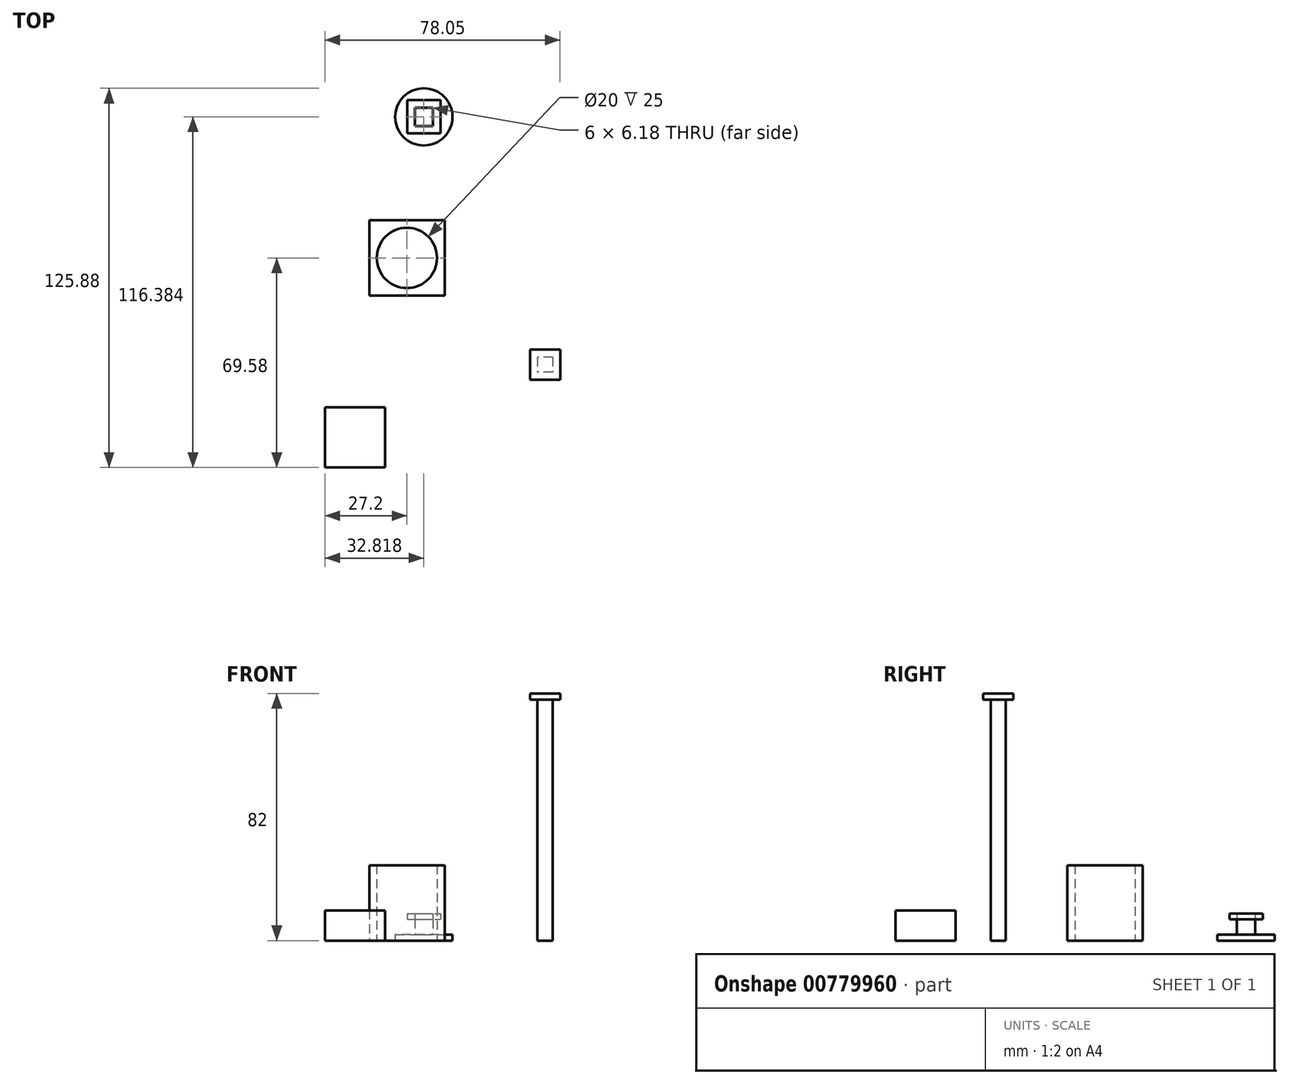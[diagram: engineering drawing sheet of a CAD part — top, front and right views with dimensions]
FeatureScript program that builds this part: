
annotation { "Feature Type Name" : "Feature", "Feature Type Description" : "" }
export const myFeature = defineFeature(function(context is Context, id is Id, definition is map)
    precondition{}
    {
        {
            var Q0;
            Q0=qCreatedBy(makeId("Top.planeOp"),FACE);
            var sketch = newSketch(context, id + "F0", { "sketchPlane" : qUnion([Q0])});
            skLineSegment(sketch, "E0.bottom", {"start": v(12.5, -12.5) * mm, "end": v(-12.5, -12.5) * mm});
            skLineSegment(sketch, "E0.top", {"start": v(12.5, 12.5) * mm, "end": v(-12.5, 12.5) * mm});
            skLineSegment(sketch, "E0.left", {"start": v(12.5, -12.5) * mm, "end": v(12.5, 12.5) * mm});
            skLineSegment(sketch, "E0.right", {"start": v(-12.5, -12.5) * mm, "end": v(-12.5, 12.5) * mm});
            skPoint(sketch, "E0.middle", {"position": v(0, 0) * mm});
            skSolve(sketch);
        }
        {
            var Q0;
            Q0=makeQuery(id+"F0.imprint","IMPRINT",FACE,{"disambiguationData":[TD([[makeQuery(id+"F0.imprint","IMPRINT",EDGE,{"derivedFrom":sQuery(id+"F0.wireOp",EDGE,"E0.bottom")}),-1.0]])]});
            extrude(context, id + "F1", {"entities" : qUnion([Q0]), "depth" : 25 * mm, "offsetDistance" : 25 * mm});
        }
        {
            var Q0;
            Q0=sQuery(id+"F0.wireOp",VERTEX,"E0.middle");
            var Q1;
            Q1=makeQuery(id+"F1.opExtrude","SWEPT_BODY",BODY,{"disambiguationData":[OSD([sQuery(id+"F0.wireOp",EDGE,"E0.bottom"),sQuery(id+"F0.wireOp",EDGE,"E0.top"),sQuery(id+"F0.wireOp",EDGE,"E0.left"),sQuery(id+"F0.wireOp",EDGE,"E0.right")])]});
            hole(context, id + "F2", {"style" : HoleStyle.SIMPLE, "endStyle" : HoleEndStyle.THROUGH, "oppositeDirection" : true, "holeDiameter" : 20 * mm, "majorDiameter" : 5 * mm, "isTappedThrough" : true, "tappedDepth" : 12 * mm, "tapClearance" : 3, "locations" : qUnion([Q0]), "scope" : qUnion([Q1])});
        }
        {
            var Q0;
            Q0=qCreatedBy(makeId("Top.planeOp"),FACE);
            var sketch = newSketch(context, id + "F3", { "sketchPlane" : qUnion([Q0])});
            skCircle(sketch, "E1", {"center": v(5.62, 46.8) * mm, "radius": 9.5 * mm});
            skSolve(sketch);
        }
        {
            var Q0;
            Q0 = qSketchRegion(id + "F3", true);
            extrude(context, id + "F4", {"entities" : qUnion([Q0]), "depth" : 2 * mm, "offsetDistance" : 25 * mm});
        }
        {
            var Q0;
            Q0=makeQuery(id+"F4.opExtrude","CAP_FACE",FACE,{"disambiguationData":[OSD([sQuery(id+"F3.wireOp",EDGE,"E1")])],"isStart":false});
            var sketch = newSketch(context, id + "F5", { "sketchPlane" : qUnion([Q0])});
            skLineSegment(sketch, "E2.bottom", {"start": v(2.62, 49.9) * mm, "end": v(8.62, 49.9) * mm});
            skLineSegment(sketch, "E2.top", {"start": v(2.62, 43.71) * mm, "end": v(8.62, 43.71) * mm});
            skLineSegment(sketch, "E2.left", {"start": v(2.62, 49.9) * mm, "end": v(2.62, 43.71) * mm});
            skLineSegment(sketch, "E2.right", {"start": v(8.62, 49.9) * mm, "end": v(8.62, 43.71) * mm});
            skPoint(sketch, "E2.middle", {"position": v(5.62, 46.8) * mm});
            skSolve(sketch);
        }
        {
            var Q0;
            Q0=makeQuery(id+"F5.imprint","IMPRINT",FACE,{"disambiguationData":[TD([[makeQuery(id+"F5.imprint","IMPRINT",EDGE,{"derivedFrom":sQuery(id+"F5.wireOp",EDGE,"E2.bottom")}),-1.0]])]});
            var Q1;
            Q1=sQuery(id+"F5.wireOp",EDGE,"E2.top");
            var Q2;
            Q2=sQuery(id+"F5.wireOp",EDGE,"E2.right");
            var Q3;
            Q3=sQuery(id+"F5.wireOp",EDGE,"E2.left");
            var Q4;
            Q4=sQuery(id+"F5.wireOp",EDGE,"E2.bottom");
            extrude(context, id + "F6", {"entities" : qUnion([Q0]), "operationType" : NewBodyOperationType.ADD, "surfaceOperationType" : NewSurfaceOperationType.ADD, "surfaceEntities" : qUnion([Q1, Q2, Q3, Q4]), "depth" : 5 * mm, "offsetDistance" : 25 * mm});
        }
        {
            var Q0;
            Q0=qCreatedBy(makeId("Top.planeOp"),FACE);
            var sketch = newSketch(context, id + "F7", { "sketchPlane" : qUnion([Q0])});
            skLineSegment(sketch, "E3.bottom", {"start": v(9.2, -50.91) * mm, "end": v(-5.8, -50.91) * mm});
            skLineSegment(sketch, "E3.top", {"start": v(9.2, -65.91) * mm, "end": v(-5.8, -65.91) * mm});
            skLineSegment(sketch, "E3.left", {"start": v(9.2, -50.91) * mm, "end": v(9.2, -65.91) * mm});
            skLineSegment(sketch, "E3.right", {"start": v(-5.8, -50.91) * mm, "end": v(-5.8, -65.91) * mm});
            skPoint(sketch, "E3.middle", {"position": v(1.7, -58.41) * mm});
            skSolve(sketch);
        }
        {
            var Q0;
            Q0 = qSketchRegion(id + "F7", true);
            extrude(context, id + "F8", {"entities" : qUnion([Q0]), "depth" : 80 * mm, "offsetDistance" : 25 * mm});
        }
        {
            var Q0;
            Q0=qCreatedBy(makeId("Top.planeOp"),FACE);
            var sketch = newSketch(context, id + "F9", { "sketchPlane" : qUnion([Q0])});
            skLineSegment(sketch, "E4.bottom", {"start": v(48.35, -32.97) * mm, "end": v(43.35, -32.97) * mm});
            skLineSegment(sketch, "E4.top", {"start": v(48.35, -37.97) * mm, "end": v(43.35, -37.97) * mm});
            skLineSegment(sketch, "E4.left", {"start": v(48.35, -32.97) * mm, "end": v(48.35, -37.97) * mm});
            skLineSegment(sketch, "E4.right", {"start": v(43.35, -32.97) * mm, "end": v(43.35, -37.97) * mm});
            skPoint(sketch, "E4.middle", {"position": v(45.85, -35.47) * mm});
            skSolve(sketch);
        }
        {
            var Q0;
            Q0 = qSketchRegion(id + "F9", true);
            extrude(context, id + "F10", {"entities" : qUnion([Q0]), "depth" : 80 * mm, "offsetDistance" : 25 * mm});
        }
        {
            var Q0;
            Q0=makeQuery(id+"F8.opExtrude","SWEPT_BODY",BODY,{"disambiguationData":[OSD([sQuery(id+"F7.wireOp",EDGE,"E3.bottom"),sQuery(id+"F7.wireOp",EDGE,"E3.top"),sQuery(id+"F7.wireOp",EDGE,"E3.left"),sQuery(id+"F7.wireOp",EDGE,"E3.right")])]});
            deleteBodies(context, id + "F11", {"entities" : qUnion([Q0])});
        }
        {
            var Q0;
            Q0=makeQuery(id+"F10.opExtrude","CAP_FACE",FACE,{"disambiguationData":[OSD([sQuery(id+"F9.wireOp",EDGE,"E4.bottom"),sQuery(id+"F9.wireOp",EDGE,"E4.top"),sQuery(id+"F9.wireOp",EDGE,"E4.left"),sQuery(id+"F9.wireOp",EDGE,"E4.right")])],"isStart":false});
            var sketch = newSketch(context, id + "F12", { "sketchPlane" : qUnion([Q0])});
            skLineSegment(sketch, "E5.bottom", {"start": v(50.85, -30.47) * mm, "end": v(40.85, -30.47) * mm});
            skLineSegment(sketch, "E5.top", {"start": v(50.85, -40.47) * mm, "end": v(40.85, -40.47) * mm});
            skLineSegment(sketch, "E5.left", {"start": v(50.85, -30.47) * mm, "end": v(50.85, -40.47) * mm});
            skLineSegment(sketch, "E5.right", {"start": v(40.85, -30.47) * mm, "end": v(40.85, -40.47) * mm});
            skPoint(sketch, "E5.middle", {"position": v(45.85, -35.47) * mm});
            skPoint(sketch, "E5.middle.positionSnap0", {"position": v(48.35, -35.47) * mm});
            skPoint(sketch, "E5.middle.positionSnap1", {"position": v(45.85, -32.97) * mm});
            skPoint(sketch, "E5.centerSnap0", {"position": v(48.35, -35.47) * mm});
            skPoint(sketch, "E5.centerSnap1", {"position": v(45.85, -32.97) * mm});
            skSolve(sketch);
        }
        {
            var Q0;
            Q0=makeQuery(id+"F12.imprint","IMPRINT",FACE,{"disambiguationData":[TD([[makeQuery(id+"F12.imprint","IMPRINT",EDGE,{"derivedFrom":makeQuery(id+"F10.opExtrude","CAP_EDGE",EDGE,{"disambiguationData":[OSD([sQuery(id+"F9.wireOp",EDGE,"E4.bottom")])],"isStart":false})}),1.0]])]});
            var Q1;
            Q1=makeQuery(id+"F12.imprint","IMPRINT",FACE,{"disambiguationData":[TD([[makeQuery(id+"F12.imprint","IMPRINT",EDGE,{"derivedFrom":sQuery(id+"F12.wireOp",EDGE,"E5.bottom")}),1.0]])]});
            extrude(context, id + "F13", {"entities" : qUnion([Q0, Q1]), "operationType" : NewBodyOperationType.ADD, "depth" : 2 * mm, "offsetDistance" : 25 * mm});
        }
        {
            var Q0;
            Q0=qCreatedBy(makeId("Top.planeOp"),FACE);
            var sketch = newSketch(context, id + "F14", { "sketchPlane" : qUnion([Q0])});
            skLineSegment(sketch, "E6.bottom", {"start": v(-7.2, -49.58) * mm, "end": v(-27.2, -49.58) * mm});
            skLineSegment(sketch, "E6.top", {"start": v(-7.2, -69.58) * mm, "end": v(-27.2, -69.58) * mm});
            skLineSegment(sketch, "E6.left", {"start": v(-7.2, -49.58) * mm, "end": v(-7.2, -69.58) * mm});
            skLineSegment(sketch, "E6.right", {"start": v(-27.2, -49.58) * mm, "end": v(-27.2, -69.58) * mm});
            skPoint(sketch, "E6.middle", {"position": v(-17.2, -59.58) * mm});
            skSolve(sketch);
        }
        {
            var Q0;
            Q0=makeQuery(id+"F14.imprint","IMPRINT",FACE,{"disambiguationData":[TD([[makeQuery(id+"F14.imprint","IMPRINT",EDGE,{"derivedFrom":sQuery(id+"F14.wireOp",EDGE,"E6.bottom")}),1.0]])]});
            extrude(context, id + "F15", {"entities" : qUnion([Q0]), "depth" : 10 * mm, "offsetDistance" : 25 * mm});
        }
        {
            var Q0;
            Q0=makeQuery(id+"F6.opExtrude","CAP_FACE",FACE,{"disambiguationData":[OSD([sQuery(id+"F5.wireOp",EDGE,"E2.bottom"),sQuery(id+"F5.wireOp",EDGE,"E2.top"),sQuery(id+"F5.wireOp",EDGE,"E2.left"),sQuery(id+"F5.wireOp",EDGE,"E2.right")])],"isStart":false});
            var sketch = newSketch(context, id + "F16", { "sketchPlane" : qUnion([Q0])});
            skPoint(sketch, "E7", {"position": v(5.62, 46.85) * mm});
            skPoint(sketch, "E7.positionSnap0", {"position": v(5.62, 49.9) * mm});
            skLineSegment(sketch, "E8.bottom", {"start": v(0.12, 52.35) * mm, "end": v(11.12, 52.35) * mm});
            skLineSegment(sketch, "E8.top", {"start": v(0.12, 41.35) * mm, "end": v(11.12, 41.35) * mm});
            skLineSegment(sketch, "E8.left", {"start": v(0.12, 52.35) * mm, "end": v(0.12, 41.35) * mm});
            skLineSegment(sketch, "E8.right", {"start": v(11.12, 52.35) * mm, "end": v(11.12, 41.35) * mm});
            skSolve(sketch);
        }
        {
            var Q0;
            Q0=makeQuery(id+"F16.imprint","IMPRINT",FACE,{"disambiguationData":[TD([[makeQuery(id+"F16.imprint","IMPRINT",EDGE,{"derivedFrom":sQuery(id+"F16.wireOp",EDGE,"E8.bottom")}),-1.0]])]});
            extrude(context, id + "F17", {"entities" : qUnion([Q0]), "depth" : 2 * mm, "offsetDistance" : 25 * mm});
        }
    });
